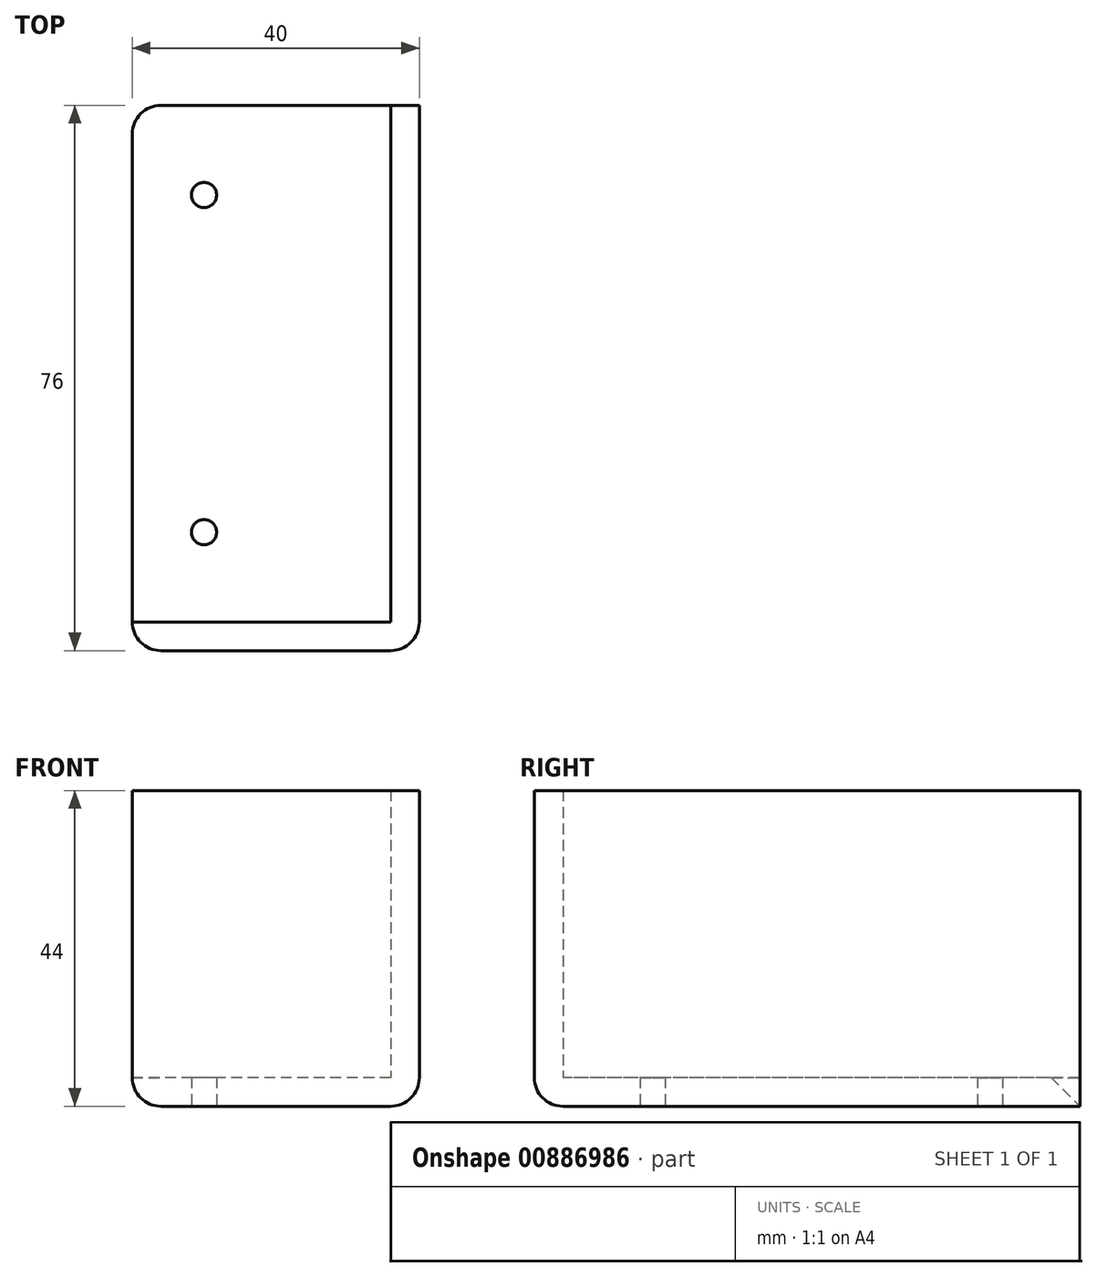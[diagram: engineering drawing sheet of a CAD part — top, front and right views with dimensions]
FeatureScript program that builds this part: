
annotation { "Feature Type Name" : "Feature", "Feature Type Description" : "" }
export const myFeature = defineFeature(function(context is Context, id is Id, definition is map)
    precondition{}
    {
        {
            var Q0;
            Q0=qCreatedBy(makeId("Top.planeOp"),FACE);
            var sketch = newSketch(context, id + "F0", { "sketchPlane" : qUnion([Q0])});
            skLineSegment(sketch, "E0.bottom", {"start": v(0, 0) * mm, "end": v(40, 0) * mm});
            skLineSegment(sketch, "E0.top", {"start": v(0, 76) * mm, "end": v(40, 76) * mm});
            skLineSegment(sketch, "E0.left", {"start": v(0, 0) * mm, "end": v(0, 76) * mm});
            skLineSegment(sketch, "E0.right", {"start": v(40, 0) * mm, "end": v(40, 76) * mm});
            skCircle(sketch, "E1", {"center": v(10, 63.5) * mm, "radius": 1.75 * mm});
            skLineSegment(sketch, "E2", {"start": v(0, 63.5) * mm, "end": v(10, 63.5) * mm, "construction": true});
            skCircle(sketch, "E3", {"center": v(10, 16.5) * mm, "radius": 1.75 * mm});
            skSolve(sketch);
        }
        {
            var Q0;
            Q0=makeQuery(id+"F0.imprint","IMPRINT",FACE,{"disambiguationData":[TD([[makeQuery(id+"F0.imprint","IMPRINT",EDGE,{"derivedFrom":sQuery(id+"F0.wireOp",EDGE,"E0.bottom")}),1.0]])]});
            var Q1;
            Q1=makeQuery(id+"F0.imprint","IMPRINT",FACE,{"disambiguationData":[TD([[makeQuery(id+"F0.imprint","IMPRINT",EDGE,{"derivedFrom":sQuery(id+"F0.wireOp",EDGE,"E1")}),1.0]])]});
            var Q2;
            Q2=makeQuery(id+"F0.imprint","IMPRINT",FACE,{"disambiguationData":[TD([[makeQuery(id+"F0.imprint","IMPRINT",EDGE,{"derivedFrom":sQuery(id+"F0.wireOp",EDGE,"E3")}),1.0]])]});
            extrude(context, id + "F1", {"entities" : qUnion([Q0, Q1, Q2]), "depth" : 44 * mm, "offsetDistance" : 25 * mm});
        }
        {
            var Q0;
            Q0=makeQuery(id+"F1.opExtrude","SWEPT_FACE",FACE,{"disambiguationData":[OSD([sQuery(id+"F0.wireOp",EDGE,"E0.left")])]});
            var sketch = newSketch(context, id + "F2", { "sketchPlane" : qUnion([Q0])});
            skLineSegment(sketch, "E4.bottom", {"start": v(-76, 44) * mm, "end": v(-4, 44) * mm});
            skLineSegment(sketch, "E4.top", {"start": v(-76, 4) * mm, "end": v(-4, 4) * mm});
            skLineSegment(sketch, "E4.left", {"start": v(-76, 44) * mm, "end": v(-76, 4) * mm});
            skLineSegment(sketch, "E4.right", {"start": v(-4, 44) * mm, "end": v(-4, 4) * mm});
            skSolve(sketch);
        }
        {
            var Q0;
            Q0=makeQuery(id+"F2.imprint","IMPRINT",FACE,{"disambiguationData":[TD([[makeQuery(id+"F2.imprint","IMPRINT",EDGE,{"derivedFrom":sQuery(id+"F2.wireOp",EDGE,"E4.bottom")}),-1.0]])]});
            var Q1;
            Q1=makeQuery(id+"F2.imprint","IMPRINT",FACE,{"disambiguationData":[TD([[makeQuery(id+"F2.imprint","IMPRINT",EDGE,{"derivedFrom":sQuery(id+"F2.wireOp",EDGE,"E4.bottom")}),1.0]])]});
            extrude(context, id + "F3", {"entities" : qUnion([Q0, Q1]), "operationType" : NewBodyOperationType.REMOVE, "oppositeDirection" : true, "depth" : 36 * mm, "offsetDistance" : 25 * mm});
        }
        {
            var Q0;
            Q0=makeQuery(id+"F1.opExtrude","SWEPT_FACE",FACE,{"disambiguationData":[OSD([sQuery(id+"F0.wireOp",EDGE,"E0.top")])]});
            var sketch = newSketch(context, id + "F4", { "sketchPlane" : qUnion([Q0])});
            skCircle(sketch, "E5", {"center": v(-29.5, 22.5) * mm, "radius": 4 * mm});
            skLineSegment(sketch, "E6", {"start": v(-29.5, 22.5) * mm, "end": v(-29.5, 0) * mm, "construction": true});
            skCircle(sketch, "E7", {"center": v(-12, 23.5) * mm, "radius": 1.5 * mm});
            skLineSegment(sketch, "E8", {"start": v(-29.5, 26.5) * mm, "end": v(0, 26.5) * mm});
            skLineSegment(sketch, "E9", {"start": v(-29.5, 18.5) * mm, "end": v(0, 18.5) * mm});
            skSolve(sketch);
        }
        {
            var Q0;
            Q0=makeQuery(id+"F4.imprint","IMPRINT",FACE,{"disambiguationData":[TD([[makeQuery(id+"F4.imprint","IMPRINT",EDGE,{"derivedFrom":sQuery(id+"F4.wireOp",EDGE,"E5")}),1.0]])]});
            var Q1;
            Q1=makeQuery(id+"F4.imprint","IMPRINT",FACE,{"disambiguationData":[TD([[makeQuery(id+"F4.imprint","IMPRINT",EDGE,{"derivedFrom":sQuery(id+"F4.wireOp",EDGE,"E7")}),-1.0]])]});
            var Q2;
            Q2=makeQuery(id+"F4.imprint","IMPRINT",FACE,{"disambiguationData":[TD([[makeQuery(id+"F4.imprint","IMPRINT",EDGE,{"derivedFrom":sQuery(id+"F4.wireOp",EDGE,"E7")}),1.0]])]});
            extrude(context, id + "F5", {"entities" : qUnion([Q0, Q1, Q2]), "operationType" : NewBodyOperationType.REMOVE, "oppositeDirection" : true, "depth" : 4 * mm, "offsetDistance" : 25 * mm});
        }
        {
            var Q0;
            Q0=makeQuery(id+"F0.imprint","IMPRINT",FACE,{"disambiguationData":[TD([[makeQuery(id+"F0.imprint","IMPRINT",EDGE,{"derivedFrom":sQuery(id+"F0.wireOp",EDGE,"E1")}),1.0]])]});
            var Q1;
            Q1=makeQuery(id+"F0.imprint","IMPRINT",FACE,{"disambiguationData":[TD([[makeQuery(id+"F0.imprint","IMPRINT",EDGE,{"derivedFrom":sQuery(id+"F0.wireOp",EDGE,"E3")}),1.0]])]});
            extrude(context, id + "F6", {"entities" : qUnion([Q0, Q1]), "operationType" : NewBodyOperationType.REMOVE, "depth" : 4 * mm, "offsetDistance" : 25 * mm});
        }
        {
            var Q0;
            Q0=makeQuery(id+"F1.opExtrude","CAP_EDGE",EDGE,{"disambiguationData":[OSD([sQuery(id+"F0.wireOp",EDGE,"E0.right")])],"isStart":true});
            var Q1;
            Q1=makeQuery(id+"F1.opExtrude","SWEPT_EDGE",EDGE,{"disambiguationData":[OSD([sQuery(id+"F0.wireOp",EDGE,"E0.bottom"),sQuery(id+"F0.wireOp",EDGE,"E0.right")])]});
            var Q2;
            Q2=makeQuery(id+"F1.opExtrude","SWEPT_EDGE",EDGE,{"disambiguationData":[OSD([sQuery(id+"F0.wireOp",EDGE,"E0.bottom"),sQuery(id+"F0.wireOp",EDGE,"E0.left")])]});
            var Q3;
            Q3=makeQuery(id+"F1.opExtrude","CAP_EDGE",EDGE,{"disambiguationData":[OSD([sQuery(id+"F0.wireOp",EDGE,"E0.bottom")])],"isStart":true});
            var Q4;
            {var subQ0=sQuery(id+"F0.wireOp",EDGE,"E0.left");var subQ1=sQuery(id+"F0.wireOp",EDGE,"E0.top");Q4=makeQuery(id+"F5.boolean.opBoolean","SPLIT",EDGE,{"disambiguationData":[TD([makeQuery(id+"F5.opExtrude","SWEPT_FACE",FACE,{"disambiguationData":[OSD([sQuery(id+"F4.wireOp",EDGE,"E8")])]})])],"derivedFrom":makeQuery(id+"F1.opExtrude","SWEPT_EDGE",EDGE,{"disambiguationData":[OSD([subQ1,subQ0])]})});}
            var Q5;
            {var subQ0=sQuery(id+"F0.wireOp",EDGE,"E0.left");var subQ1=sQuery(id+"F0.wireOp",EDGE,"E0.top");Q5=makeQuery(id+"F5.boolean.opBoolean","SPLIT",EDGE,{"disambiguationData":[TD([makeQuery(id+"F5.opExtrude","SWEPT_FACE",FACE,{"disambiguationData":[OSD([sQuery(id+"F4.wireOp",EDGE,"E9")])]})])],"derivedFrom":makeQuery(id+"F1.opExtrude","SWEPT_EDGE",EDGE,{"disambiguationData":[OSD([subQ1,subQ0])]})});}
            var Q6;
            Q6=makeQuery(id+"F1.opExtrude","CAP_EDGE",EDGE,{"disambiguationData":[OSD([sQuery(id+"F0.wireOp",EDGE,"E0.left")])],"isStart":true});
            fillet(context, id + "F7", {"entities" : qUnion([Q0, Q1, Q2, Q3, Q4, Q5, Q6]), "radius" : 4 * mm, "tangentPropagation" : true, "allowEdgeOverflow" : false});
        }
    });
